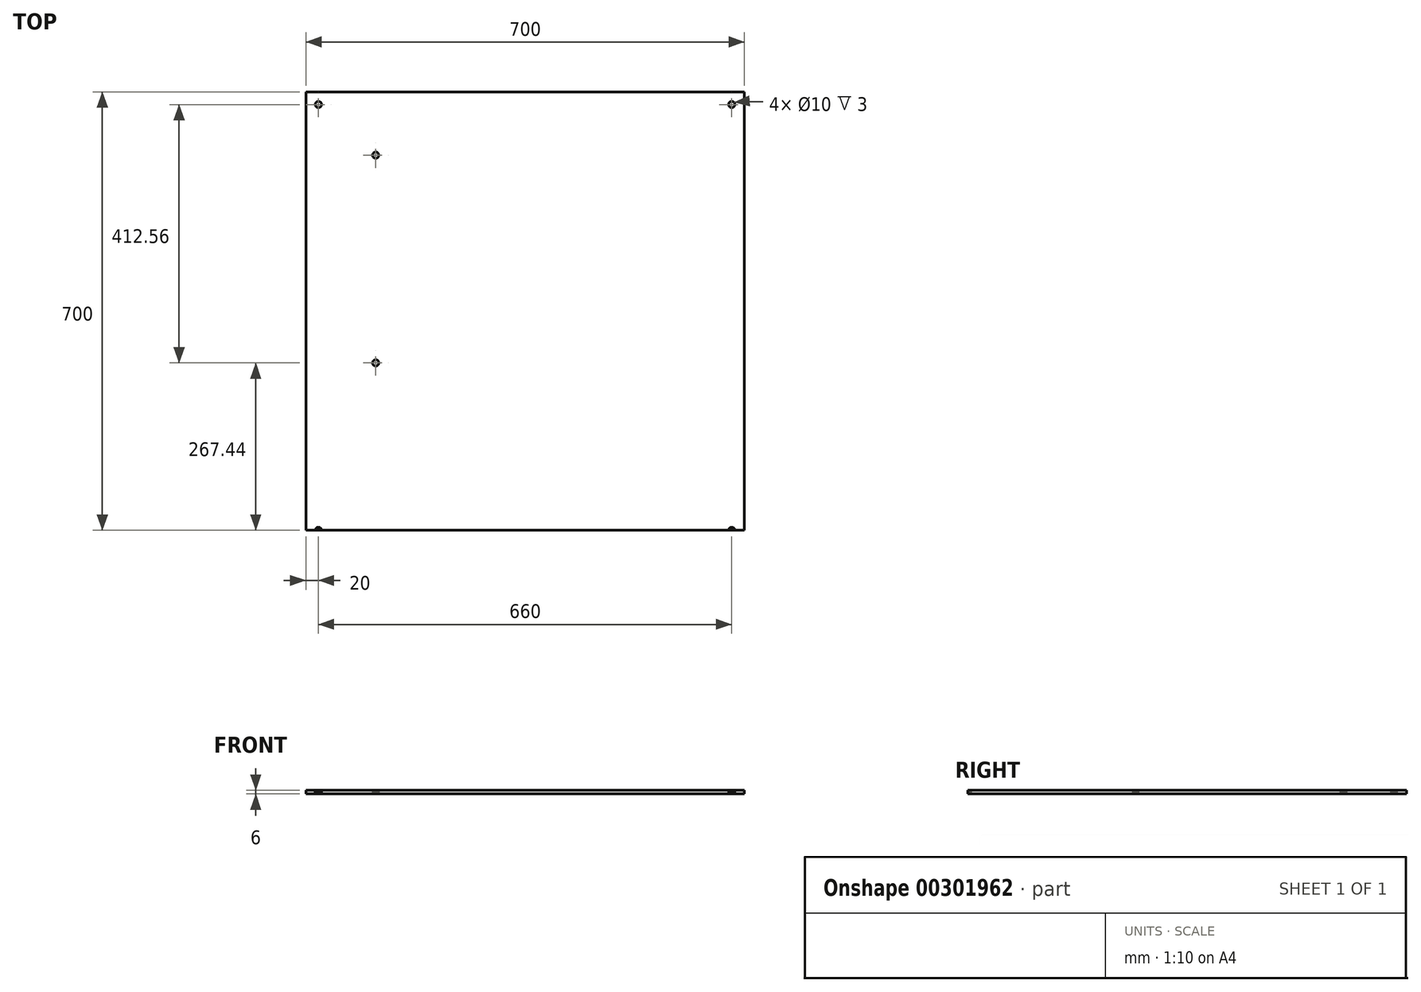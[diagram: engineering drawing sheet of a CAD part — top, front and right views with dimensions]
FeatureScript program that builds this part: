
annotation { "Feature Type Name" : "Feature", "Feature Type Description" : "" }
export const myFeature = defineFeature(function(context is Context, id is Id, definition is map)
    precondition{}
    {
        {
            var Q0;
            Q0=qCreatedBy(makeId("Top.planeOp"),FACE);
            var sketch = newSketch(context, id + "F0", { "sketchPlane" : qUnion([Q0])});
            skLineSegment(sketch, "E0.bottom", {"start": v(350, 350) * mm, "end": v(-350, 350) * mm});
            skLineSegment(sketch, "E0.top", {"start": v(350, -350) * mm, "end": v(-350, -350) * mm});
            skLineSegment(sketch, "E0.left", {"start": v(350, 350) * mm, "end": v(350, -350) * mm});
            skLineSegment(sketch, "E0.right", {"start": v(-350, 350) * mm, "end": v(-350, -350) * mm});
            skPoint(sketch, "E0.middle", {"position": v(0, 0) * mm});
            skPoint(sketch, "E1", {"position": v(-330, 330) * mm});
            skPoint(sketch, "E2", {"position": v(330, 330) * mm});
            skPoint(sketch, "E3", {"position": v(330, -350) * mm});
            skPoint(sketch, "E4", {"position": v(-330, -350) * mm});
            skPoint(sketch, "E5", {"position": v(-238.5, 249.04) * mm});
            skPoint(sketch, "E6", {"position": v(-238.5, -82.56) * mm});
            skSolve(sketch);
        }
        {
            var Q0;
            Q0=makeQuery(id+"F0.imprint","IMPRINT",FACE,{"disambiguationData":[TD([[makeQuery(id+"F0.imprint","IMPRINT",EDGE,{"derivedFrom":sQuery(id+"F0.wireOp",EDGE,"E0.bottom")}),1.0]])]});
            extrude(context, id + "F1", {"entities" : qUnion([Q0]), "endBound" : BoundingType.SYMMETRIC, "depth" : 6 * mm});
        }
        {
            var Q0;
            Q0=sQuery(id+"F0.wireOp",VERTEX,"E1");
            var Q1;
            Q1=sQuery(id+"F0.wireOp",VERTEX,"E2");
            var Q2;
            Q2=sQuery(id+"F0.wireOp",VERTEX,"E3");
            var Q3;
            Q3=sQuery(id+"F0.wireOp",VERTEX,"E4");
            var Q4;
            Q4=sQuery(id+"F0.wireOp",VERTEX,"E5");
            var Q5;
            Q5=sQuery(id+"F0.wireOp",VERTEX,"E6");
            var Q6;
            Q6=makeQuery(id+"F1.opExtrude","SWEPT_BODY",BODY,{"disambiguationData":[OSD([sQuery(id+"F0.wireOp",EDGE,"E0.bottom"),sQuery(id+"F0.wireOp",EDGE,"E0.top"),sQuery(id+"F0.wireOp",EDGE,"E0.left"),sQuery(id+"F0.wireOp",EDGE,"E0.right")])]});
            hole(context, id + "F2", {"style" : HoleStyle.SIMPLE, "endStyle" : HoleEndStyle.THROUGH, "oppositeDirection" : true, "holeDiameter" : 10 * mm, "tappedDepth" : 12 * mm, "tapClearance" : 3, "locations" : qUnion([Q0, Q1, Q2, Q3, Q4, Q5]), "scope" : qUnion([Q6])});
        }
    });
